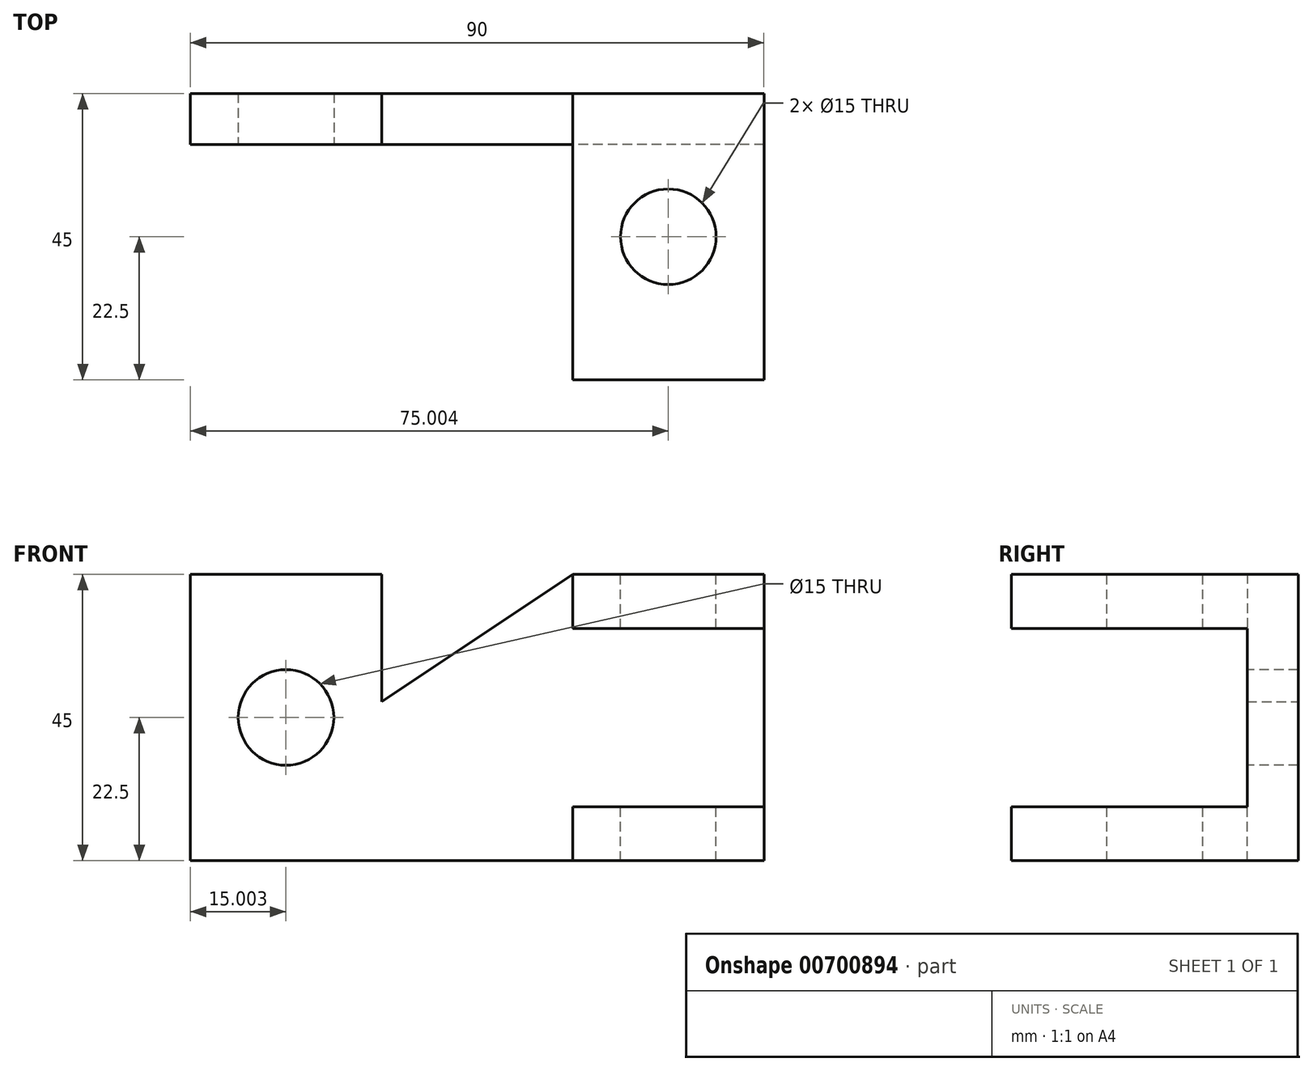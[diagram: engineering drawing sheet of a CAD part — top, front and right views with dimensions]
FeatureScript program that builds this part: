
annotation { "Feature Type Name" : "Feature", "Feature Type Description" : "" }
export const myFeature = defineFeature(function(context is Context, id is Id, definition is map)
    precondition{}
    {
        {
            var Q0;
            Q0=qCreatedBy(makeId("Front.planeOp"),FACE);
            var sketch = newSketch(context, id + "F0", { "sketchPlane" : qUnion([Q0])});
            skLineSegment(sketch, "E0", {"start": v(48.25, -28.97) * mm, "end": v(48.25, 16.03) * mm});
            skLineSegment(sketch, "E1", {"start": v(48.25, 16.03) * mm, "end": v(18.25, 16.03) * mm});
            skLineSegment(sketch, "E2", {"start": v(48.25, -28.97) * mm, "end": v(-41.75, -28.97) * mm});
            skLineSegment(sketch, "E3", {"start": v(-41.75, -28.97) * mm, "end": v(-41.75, 16.03) * mm});
            skLineSegment(sketch, "E4", {"start": v(-41.75, 16.03) * mm, "end": v(-11.75, 16.03) * mm});
            skLineSegment(sketch, "E5", {"start": v(-11.75, 16.03) * mm, "end": v(-11.75, -3.97) * mm});
            skLineSegment(sketch, "E6", {"start": v(-11.75, -3.97) * mm, "end": v(18.25, 16.03) * mm});
            skSolve(sketch);
        }
        {
            var Q0;
            Q0=makeQuery(id+"F0.imprint","IMPRINT",FACE,{"disambiguationData":[TD([[makeQuery(id+"F0.imprint","IMPRINT",EDGE,{"derivedFrom":sQuery(id+"F0.wireOp",EDGE,"E0")}),1.0]])]});
            extrude(context, id + "F1", {"entities" : qUnion([Q0]), "depth" : 8 * mm, "offsetDistance" : 25 * mm});
        }
        {
            var Q0;
            Q0=makeQuery(id+"F1.opExtrude","CAP_FACE",FACE,{"disambiguationData":[OSD([sQuery(id+"F0.wireOp",EDGE,"E0"),sQuery(id+"F0.wireOp",EDGE,"E1"),sQuery(id+"F0.wireOp",EDGE,"E2"),sQuery(id+"F0.wireOp",EDGE,"E3"),sQuery(id+"F0.wireOp",EDGE,"E4"),sQuery(id+"F0.wireOp",EDGE,"E5"),sQuery(id+"F0.wireOp",EDGE,"E6")])],"isStart":false});
            var sketch = newSketch(context, id + "F2", { "sketchPlane" : qUnion([Q0])});
            skLineSegment(sketch, "E7.bottom", {"start": v(48.25, 16.03) * mm, "end": v(18.25, 16.03) * mm});
            skLineSegment(sketch, "E7.top", {"start": v(48.25, 7.53) * mm, "end": v(18.25, 7.53) * mm});
            skLineSegment(sketch, "E7.left", {"start": v(48.25, 16.03) * mm, "end": v(48.25, 7.53) * mm});
            skLineSegment(sketch, "E7.right", {"start": v(18.25, 16.03) * mm, "end": v(18.25, 7.53) * mm});
            skLineSegment(sketch, "E8.bottom", {"start": v(48.25, -28.97) * mm, "end": v(18.25, -28.97) * mm});
            skLineSegment(sketch, "E8.top", {"start": v(48.25, -20.47) * mm, "end": v(18.25, -20.47) * mm});
            skLineSegment(sketch, "E8.left", {"start": v(48.25, -28.97) * mm, "end": v(48.25, -20.47) * mm});
            skLineSegment(sketch, "E8.right", {"start": v(18.25, -28.97) * mm, "end": v(18.25, -20.47) * mm});
            skSolve(sketch);
        }
        {
            var Q0;
            Q0=makeQuery(id+"F2.imprint","IMPRINT",FACE,{"disambiguationData":[TD([[makeQuery(id+"F2.imprint","IMPRINT",EDGE,{"derivedFrom":sQuery(id+"F2.wireOp",EDGE,"E7.bottom")}),1.0]])]});
            var Q1;
            Q1=makeQuery(id+"F2.imprint","IMPRINT",FACE,{"disambiguationData":[TD([[makeQuery(id+"F2.imprint","IMPRINT",EDGE,{"derivedFrom":sQuery(id+"F2.wireOp",EDGE,"E8.bottom")}),-1.0]])]});
            extrude(context, id + "F3", {"entities" : qUnion([Q0, Q1]), "operationType" : NewBodyOperationType.ADD, "depth" : 37 * mm, "offsetDistance" : 25 * mm});
        }
        {
            var Q0;
            Q0=makeQuery(id+"F3.boolean.opBoolean","MERGE",FACE,{"derivedFrom":[makeQuery(id+"F1.opExtrude","SWEPT_FACE",FACE,{"disambiguationData":[OSD([sQuery(id+"F0.wireOp",EDGE,"E1")])]}),makeQuery(id+"F3.opExtrude","SWEPT_FACE",FACE,{"disambiguationData":[OSD([sQuery(id+"F2.wireOp",EDGE,"E7.bottom")])]})]});
            var sketch = newSketch(context, id + "F4", { "sketchPlane" : qUnion([Q0])});
            skCircle(sketch, "E9", {"center": v(33.25, -22.5) * mm, "radius": 7.5 * mm});
            skSolve(sketch);
        }
        {
            var Q0;
            Q0=makeQuery(id+"F4.imprint","IMPRINT",FACE,{"disambiguationData":[TD([[makeQuery(id+"F4.imprint","IMPRINT",EDGE,{"derivedFrom":sQuery(id+"F4.wireOp",EDGE,"E9")}),1.0]])]});
            extrude(context, id + "F5", {"entities" : qUnion([Q0]), "operationType" : NewBodyOperationType.REMOVE, "endBound" : BoundingType.THROUGH_ALL, "oppositeDirection" : true, "depth" : 25 * mm, "offsetDistance" : 25 * mm});
        }
        {
            var Q0;
            Q0=makeQuery(id+"F1.opExtrude","CAP_FACE",FACE,{"disambiguationData":[OSD([sQuery(id+"F0.wireOp",EDGE,"E0"),sQuery(id+"F0.wireOp",EDGE,"E1"),sQuery(id+"F0.wireOp",EDGE,"E2"),sQuery(id+"F0.wireOp",EDGE,"E3"),sQuery(id+"F0.wireOp",EDGE,"E4"),sQuery(id+"F0.wireOp",EDGE,"E5"),sQuery(id+"F0.wireOp",EDGE,"E6")])],"isStart":false});
            var sketch = newSketch(context, id + "F6", { "sketchPlane" : qUnion([Q0])});
            skCircle(sketch, "E10", {"center": v(-26.75, -6.47) * mm, "radius": 7.5 * mm});
            skSolve(sketch);
        }
        {
            var Q0;
            Q0 = qSketchRegion(id + "F6", true);
            extrude(context, id + "F7", {"entities" : qUnion([Q0]), "operationType" : NewBodyOperationType.REMOVE, "endBound" : BoundingType.THROUGH_ALL, "oppositeDirection" : true, "depth" : 25 * mm, "offsetDistance" : 25 * mm});
        }
    });
